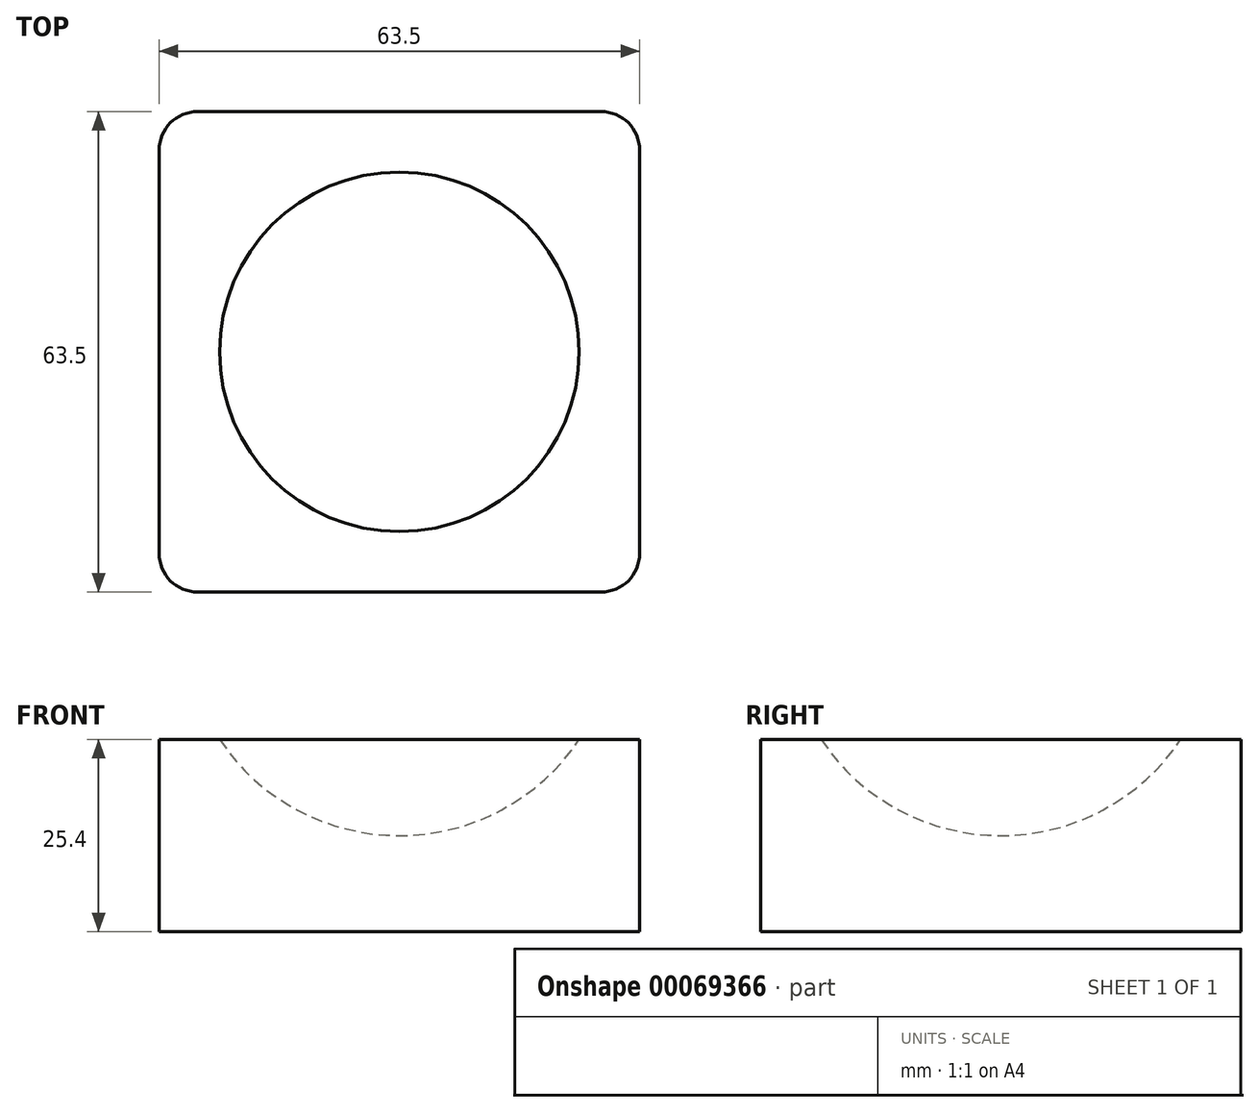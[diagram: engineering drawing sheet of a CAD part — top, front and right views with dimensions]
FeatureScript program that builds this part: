
annotation { "Feature Type Name" : "Feature", "Feature Type Description" : "" }
export const myFeature = defineFeature(function(context is Context, id is Id, definition is map)
    precondition{}
    {
        {
            var Q0;
            Q0=qCreatedBy(makeId("Top.planeOp"),FACE);
            var sketch = newSketch(context, id + "F0", { "sketchPlane" : qUnion([Q0])});
            skPoint(sketch, "E0.0", {"position": v(0, 0) * mm});
            skLineSegment(sketch, "E1.bottom", {"start": v(0, 0) * mm, "end": v(63.5, 0) * mm});
            skLineSegment(sketch, "E1.top", {"start": v(0, -63.5) * mm, "end": v(63.5, -63.5) * mm});
            skLineSegment(sketch, "E1.left", {"start": v(0, 0) * mm, "end": v(0, -63.5) * mm});
            skLineSegment(sketch, "E1.right", {"start": v(63.5, 0) * mm, "end": v(63.5, -63.5) * mm});
            skSolve(sketch);
        }
        {
            var Q0;
            Q0=makeQuery(id+"F0.imprint","IMPRINT",FACE,{"disambiguationData":[TD([[makeQuery(id+"F0.imprint","IMPRINT",EDGE,{"derivedFrom":sQuery(id+"F0.wireOp",EDGE,"E1.bottom")}),-1.0]])]});
            extrude(context, id + "F1", {"entities" : qUnion([Q0]), "depth" : 44.45 * mm});
        }
        {
            var Q0;
            Q0=makeQuery(id+"F1.opExtrude","CAP_FACE",FACE,{"disambiguationData":[OSD([sQuery(id+"F0.wireOp",EDGE,"E1.bottom"),sQuery(id+"F0.wireOp",EDGE,"E1.top"),sQuery(id+"F0.wireOp",EDGE,"E1.left"),sQuery(id+"F0.wireOp",EDGE,"E1.right")])],"isStart":false});
            cPlane(context, id + "F2", {"entities" : qUnion([Q0]), "cplaneType" : CPlaneType.OFFSET, "offset" : 15.88 * mm, "width" : 152.4 * mm, "height" : 152.4 * mm});
        }
        {
            var Q0;
            Q0=qCreatedBy(id+"F2.planeOp",FACE);
            var sketch = newSketch(context, id + "F3", { "sketchPlane" : qUnion([Q0])});
            skLineSegment(sketch, "E2.0.0", {"start": v(63.5, 0) * mm, "end": v(0, 0) * mm});
            skLineSegment(sketch, "E2.0.1", {"start": v(0, 0) * mm, "end": v(0, -63.5) * mm});
            skLineSegment(sketch, "E2.0.2", {"start": v(0, -63.5) * mm, "end": v(63.5, -63.5) * mm});
            skLineSegment(sketch, "E2.0.3", {"start": v(63.5, -63.5) * mm, "end": v(63.5, 0) * mm});
            skPoint(sketch, "E3", {"position": v(31.75, -31.75) * mm});
            skLineSegment(sketch, "E4", {"start": v(3.17, -31.75) * mm, "end": v(60.33, -31.75) * mm});
            skArc(sketch, "E5", {"start": v(3.17, -31.75) * mm, "mid": v(31.75, -60.33) * mm, "end": v(60.33, -31.75) * mm});
            skSolve(sketch);
        }
        {
            var Q0;
            Q0=makeQuery(id+"F3.imprint","IMPRINT",FACE,{"disambiguationData":[TD([[makeQuery(id+"F3.imprint","IMPRINT",EDGE,{"derivedFrom":sQuery(id+"F3.wireOp",EDGE,"E4")}),-1.0]])]});
            var Q1;
            Q1=sQuery(id+"F3.wireOp",EDGE,"E4");
            revolve(context, id + "F4", {"operationType" : NewBodyOperationType.REMOVE, "entities" : qUnion([Q0]), "axis" : qUnion([Q1]), "revolveType" : RevolveType.FULL, "oppositeDirection" : true});
        }
        {
            var Q0;
            Q0=makeQuery(id+"F1.opExtrude","SWEPT_FACE",FACE,{"disambiguationData":[OSD([sQuery(id+"F0.wireOp",EDGE,"E1.top")])]});
            var sketch = newSketch(context, id + "F5", { "sketchPlane" : qUnion([Q0])});
            skLineSegment(sketch, "E6.bottom", {"start": v(63.5, 0) * mm, "end": v(0, 0) * mm});
            skLineSegment(sketch, "E6.top", {"start": v(63.5, 19.05) * mm, "end": v(0, 19.05) * mm});
            skLineSegment(sketch, "E6.left", {"start": v(63.5, 0) * mm, "end": v(63.5, 19.05) * mm});
            skLineSegment(sketch, "E6.right", {"start": v(0, 0) * mm, "end": v(0, 19.05) * mm});
            skSolve(sketch);
        }
        {
            var Q0;
            Q0=makeQuery(id+"F5.imprint","IMPRINT",FACE,{"disambiguationData":[TD([[makeQuery(id+"F5.imprint","IMPRINT",EDGE,{"derivedFrom":sQuery(id+"F5.wireOp",EDGE,"E6.bottom")}),1.0]])]});
            extrude(context, id + "F6", {"entities" : qUnion([Q0]), "operationType" : NewBodyOperationType.REMOVE, "endBound" : BoundingType.THROUGH_ALL, "oppositeDirection" : true, "depth" : 25.4 * mm});
        }
        {
            var Q0;
            Q0=makeQuery(id+"F1.opExtrude","SWEPT_EDGE",EDGE,{"disambiguationData":[OSD([sQuery(id+"F0.wireOp",EDGE,"E1.top"),sQuery(id+"F0.wireOp",EDGE,"E1.right")])]});
            var Q1;
            Q1=makeQuery(id+"F1.opExtrude","SWEPT_EDGE",EDGE,{"disambiguationData":[OSD([sQuery(id+"F0.wireOp",EDGE,"E1.bottom"),sQuery(id+"F0.wireOp",EDGE,"E1.right")])]});
            var Q2;
            Q2=makeQuery(id+"F1.opExtrude","SWEPT_EDGE",EDGE,{"disambiguationData":[OSD([sQuery(id+"F0.wireOp",EDGE,"E1.bottom"),sQuery(id+"F0.wireOp",EDGE,"E1.left")])]});
            var Q3;
            Q3=makeQuery(id+"F1.opExtrude","SWEPT_EDGE",EDGE,{"disambiguationData":[OSD([sQuery(id+"F0.wireOp",EDGE,"E1.top"),sQuery(id+"F0.wireOp",EDGE,"E1.left")])]});
            fillet(context, id + "F7", {"entities" : qUnion([Q0, Q1, Q2, Q3]), "radius" : 5.08 * mm, "tangentPropagation" : true, "allowEdgeOverflow" : false});
        }
    });
